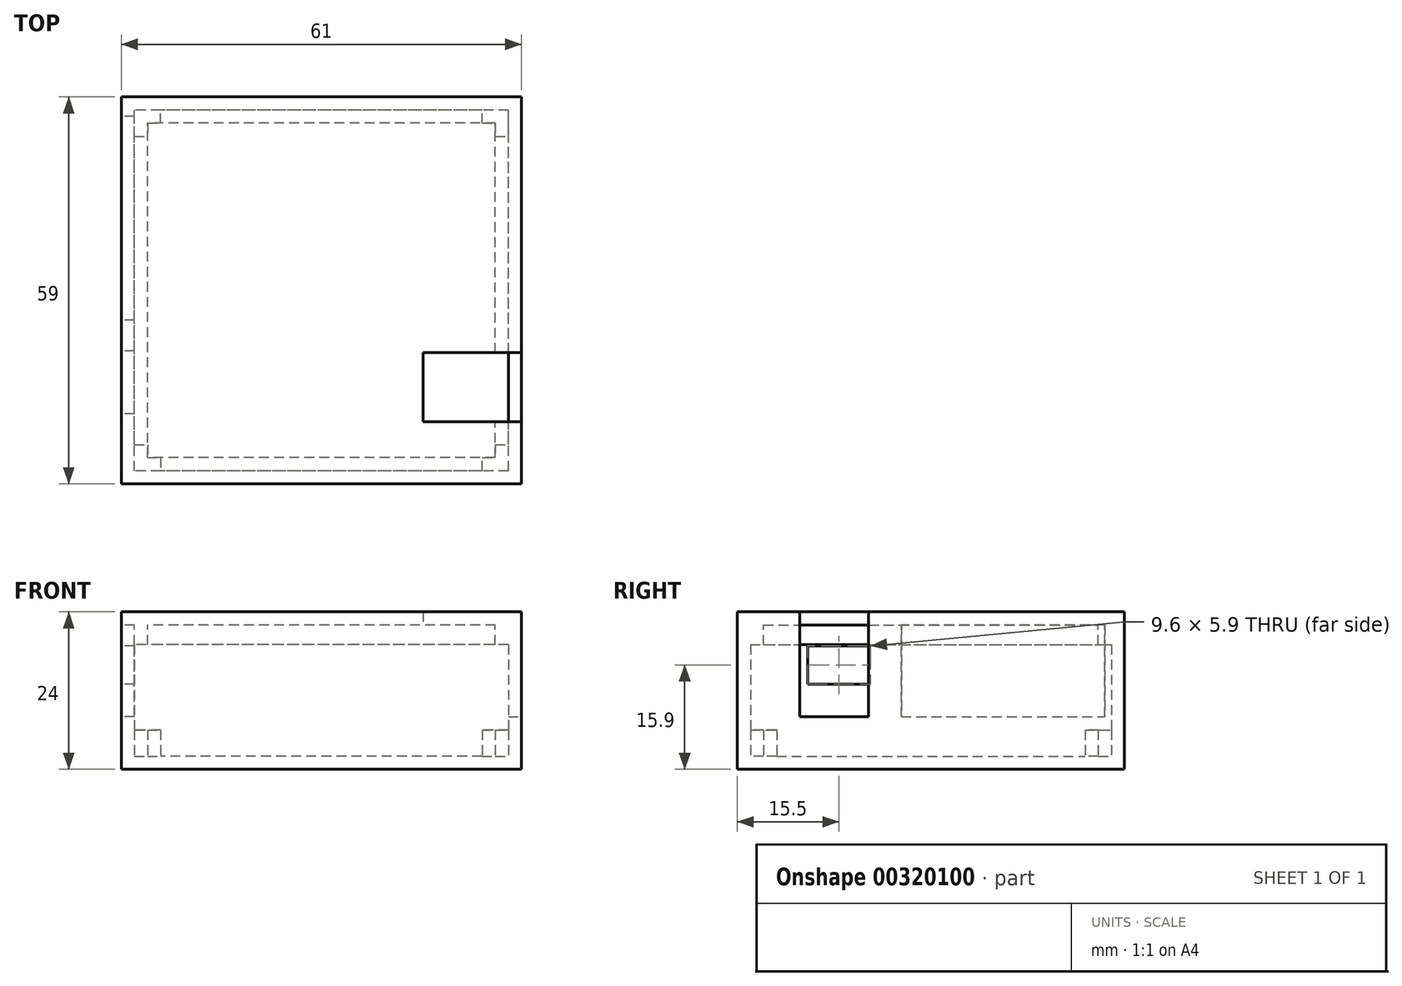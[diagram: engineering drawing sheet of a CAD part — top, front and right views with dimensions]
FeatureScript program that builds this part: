
annotation { "Feature Type Name" : "Feature", "Feature Type Description" : "" }
export const myFeature = defineFeature(function(context is Context, id is Id, definition is map)
    precondition{}
    {
        {
            var Q0;
            Q0=qCreatedBy(makeId("Top.planeOp"),FACE);
            var sketch = newSketch(context, id + "F0", { "sketchPlane" : qUnion([Q0])});
            skLineSegment(sketch, "E0.bottom", {"start": v(28.5, -27.5) * mm, "end": v(-28.5, -27.5) * mm});
            skLineSegment(sketch, "E0.top", {"start": v(28.5, 27.5) * mm, "end": v(-28.5, 27.5) * mm});
            skLineSegment(sketch, "E0.left", {"start": v(28.5, -27.5) * mm, "end": v(28.5, 27.5) * mm});
            skLineSegment(sketch, "E0.right", {"start": v(-28.5, -27.5) * mm, "end": v(-28.5, 27.5) * mm});
            skPoint(sketch, "E0.middle", {"position": v(0, 0) * mm});
            skLineSegment(sketch, "E1.bottom", {"start": v(-30.5, -29.5) * mm, "end": v(30.5, -29.5) * mm});
            skLineSegment(sketch, "E1.top", {"start": v(-30.5, 29.5) * mm, "end": v(30.5, 29.5) * mm});
            skLineSegment(sketch, "E1.left", {"start": v(-30.5, -29.5) * mm, "end": v(-30.5, 29.5) * mm});
            skLineSegment(sketch, "E1.right", {"start": v(30.5, -29.5) * mm, "end": v(30.5, 29.5) * mm});
            skLineSegment(sketch, "E2.bottom", {"start": v(-26.5, 25.5) * mm, "end": v(-24.5, 25.5) * mm});
            skLineSegment(sketch, "E2.top", {"start": v(-26.5, -25.5) * mm, "end": v(-24.5, -25.5) * mm});
            skLineSegment(sketch, "E2.left", {"start": v(-26.5, 25.5) * mm, "end": v(-26.5, 23.5) * mm});
            skLineSegment(sketch, "E2.right", {"start": v(26.5, 25.5) * mm, "end": v(26.5, 23.5) * mm});
            skLineSegment(sketch, "E3", {"start": v(-30.5, -4.5) * mm, "end": v(-26.5, -4.5) * mm});
            skLineSegment(sketch, "E4", {"start": v(-28.5, 23.5) * mm, "end": v(-26.5, 23.5) * mm});
            skLineSegment(sketch, "E5", {"start": v(-24.5, 25.5) * mm, "end": v(-24.5, 27.5) * mm});
            skLineSegment(sketch, "E6", {"start": v(24.5, 25.5) * mm, "end": v(24.5, 27.5) * mm});
            skLineSegment(sketch, "E7", {"start": v(26.5, 23.5) * mm, "end": v(28.5, 23.5) * mm});
            skLineSegment(sketch, "E8", {"start": v(-28.5, -23.5) * mm, "end": v(-26.5, -23.5) * mm});
            skLineSegment(sketch, "E9", {"start": v(-24.5, -25.5) * mm, "end": v(-24.5, -27.5) * mm});
            skLineSegment(sketch, "E10", {"start": v(26.5, -23.5) * mm, "end": v(28.5, -23.5) * mm});
            skLineSegment(sketch, "E11", {"start": v(24.5, -27.5) * mm, "end": v(24.5, -25.5) * mm});
            skLineSegment(sketch, "E12.trimOffspring", {"start": v(26.5, -23.5) * mm, "end": v(26.5, -25.5) * mm});
            skLineSegment(sketch, "E13.trimOffspring", {"start": v(24.5, 25.5) * mm, "end": v(26.5, 25.5) * mm});
            skLineSegment(sketch, "E14.trimOffspring", {"start": v(-26.5, -23.5) * mm, "end": v(-26.5, -25.5) * mm});
            skLineSegment(sketch, "E15.trimOffspring", {"start": v(24.5, -25.5) * mm, "end": v(26.5, -25.5) * mm});
            skSolve(sketch);
        }
        {
            var Q0;
            Q0=makeQuery(id+"F0.imprint","IMPRINT",FACE,{"disambiguationData":[TD([[makeQuery(id+"F0.imprint","IMPRINT",EDGE,{"derivedFrom":sQuery(id+"F0.wireOp",EDGE,"E0.bottom")}),1.0]])]});
            var Q1;
            Q1=makeQuery(id+"F0.imprint","IMPRINT",FACE,{"disambiguationData":[TD([[makeQuery(id+"F0.imprint","IMPRINT",EDGE,{"derivedFrom":sQuery(id+"F0.wireOp",EDGE,"E0.bottom")}),-1.0]])]});
            var Q2;
            Q2=makeQuery(id+"F0.imprint","IMPRINT",FACE,{"disambiguationData":[TD([[makeQuery(id+"F0.imprint","IMPRINT",EDGE,{"derivedFrom":sQuery(id+"F0.wireOp",EDGE,"E2.bottom")}),-1.0]])]});
            var Q3;
            Q3=makeQuery(id+"F0.imprint","IMPRINT",FACE,{"disambiguationData":[TD([[makeQuery(id+"F0.imprint","IMPRINT",EDGE,{"derivedFrom":sQuery(id+"F0.wireOp",EDGE,"E2.right")}),1.0]])]});
            var Q4;
            Q4=makeQuery(id+"F0.imprint","IMPRINT",FACE,{"disambiguationData":[TD([[makeQuery(id+"F0.imprint","IMPRINT",EDGE,{"derivedFrom":sQuery(id+"F0.wireOp",EDGE,"E2.bottom")}),1.0]])]});
            var Q5;
            Q5=sQuery(id+"F0.wireOp",EDGE,"E1.right");
            var Q6;
            Q6=sQuery(id+"F0.wireOp",EDGE,"E1.top");
            var Q7;
            Q7=sQuery(id+"F0.wireOp",EDGE,"E1.left");
            var Q8;
            Q8=sQuery(id+"F0.wireOp",EDGE,"E1.bottom");
            extrude(context, id + "F1", {"entities" : qUnion([Q0, Q1, Q2, Q3, Q4]), "surfaceEntities" : qUnion([Q5, Q6, Q7, Q8]), "depth" : -2 * mm});
        }
        {
            var Q0;
            Q0 = qSketchRegion(id + "F0", true);
            extrude(context, id + "F2", {"entities" : qUnion([Q0]), "operationType" : NewBodyOperationType.ADD, "depth" : 20 * mm});
        }
        {
            var Q0;
            Q0=qCreatedBy(makeId("Right.planeOp"),FACE);
            cPlane(context, id + "F3", {"entities" : qUnion([Q0]), "cplaneType" : CPlaneType.OFFSET, "offset" : 61 / 2 * mm, "oppositeDirection" : true, "width" : 150 * mm, "height" : 150 * mm});
        }
        {
            var Q0;
            Q0=qCreatedBy(id+"F3.planeOp",FACE);
            var sketch = newSketch(context, id + "F4", { "sketchPlane" : qUnion([Q0])});
            skLineSegment(sketch, "E16.bottom", {"start": v(26.5, 20) * mm, "end": v(-4.5, 20) * mm});
            skLineSegment(sketch, "E16.top", {"start": v(26.5, 6) * mm, "end": v(-4.5, 6) * mm});
            skLineSegment(sketch, "E16.left", {"start": v(26.5, 20) * mm, "end": v(26.5, 6) * mm});
            skLineSegment(sketch, "E16.right", {"start": v(-4.5, 20) * mm, "end": v(-4.5, 6) * mm});
            skLineSegment(sketch, "E17.bottom", {"start": v(-18.8, 10.95) * mm, "end": v(-9.2, 10.95) * mm});
            skLineSegment(sketch, "E17.top", {"start": v(-18.8, 16.85) * mm, "end": v(-9.2, 16.85) * mm});
            skLineSegment(sketch, "E17.left", {"start": v(-18.8, 10.95) * mm, "end": v(-18.8, 16.85) * mm});
            skLineSegment(sketch, "E17.right", {"start": v(-9.2, 10.95) * mm, "end": v(-9.2, 16.85) * mm});
            skPoint(sketch, "E17.middle", {"position": v(-14, 13.9) * mm});
            skSolve(sketch);
        }
        {
            var Q0;
            Q0=makeQuery(id+"F4.imprint","IMPRINT",FACE,{"disambiguationData":[TD([[makeQuery(id+"F4.imprint","IMPRINT",EDGE,{"derivedFrom":sQuery(id+"F4.wireOp",EDGE,"E16.bottom")}),1.0]])]});
            extrude(context, id + "F5", {"entities" : qUnion([Q0]), "operationType" : NewBodyOperationType.REMOVE, "endBound" : BoundingType.UP_TO_NEXT, "depth" : 19 * mm});
        }
        {
            var Q0;
            Q0=qCreatedBy(makeId("Right.planeOp"),FACE);
            cPlane(context, id + "F6", {"entities" : qUnion([Q0]), "cplaneType" : CPlaneType.OFFSET, "offset" : 30.5 * mm, "width" : 150 * mm, "height" : 150 * mm});
        }
        {
            var Q0;
            Q0=qCreatedBy(id+"F6.planeOp",FACE);
            var sketch = newSketch(context, id + "F7", { "sketchPlane" : qUnion([Q0])});
            skLineSegment(sketch, "E18.bottom", {"start": v(-20, 20) * mm, "end": v(-9.5, 20) * mm});
            skLineSegment(sketch, "E18.top", {"start": v(-20, 6) * mm, "end": v(-9.5, 6) * mm});
            skLineSegment(sketch, "E18.left", {"start": v(-20, 20) * mm, "end": v(-20, 6) * mm});
            skLineSegment(sketch, "E18.right", {"start": v(-9.5, 20) * mm, "end": v(-9.5, 6) * mm});
            skSolve(sketch);
        }
        {
            var Q0;
            Q0=makeQuery(id+"F7.imprint","IMPRINT",FACE,{"disambiguationData":[TD([[makeQuery(id+"F7.imprint","IMPRINT",EDGE,{"derivedFrom":sQuery(id+"F7.wireOp",EDGE,"E18.bottom")}),-1.0]])]});
            extrude(context, id + "F8", {"entities" : qUnion([Q0]), "operationType" : NewBodyOperationType.REMOVE, "endBound" : BoundingType.UP_TO_NEXT, "oppositeDirection" : true, "depth" : 7 * mm});
        }
        {
            var Q0;
            Q0=makeQuery(id+"F4.imprint","IMPRINT",FACE,{"disambiguationData":[TD([[makeQuery(id+"F4.imprint","IMPRINT",EDGE,{"derivedFrom":sQuery(id+"F4.wireOp",EDGE,"E17.bottom")}),1.0]])]});
            extrude(context, id + "F9", {"entities" : qUnion([Q0]), "operationType" : NewBodyOperationType.REMOVE, "depth" : 25 * mm});
        }
        {
            var Q0;
            Q0=qCreatedBy(makeId("Top.planeOp"),FACE);
            cPlane(context, id + "F10", {"entities" : qUnion([Q0]), "cplaneType" : CPlaneType.OFFSET, "offset" : 20 * mm, "width" : 150 * mm, "height" : 150 * mm});
        }
        {
            var Q0;
            Q0=qCreatedBy(id+"F10.planeOp",FACE);
            var sketch = newSketch(context, id + "F11", { "sketchPlane" : qUnion([Q0])});
            skLineSegment(sketch, "E19.bottom", {"start": v(28.5, -27.5) * mm, "end": v(-28.5, -27.5) * mm});
            skLineSegment(sketch, "E19.top", {"start": v(28.5, 27.5) * mm, "end": v(-28.5, 27.5) * mm});
            skLineSegment(sketch, "E19.left", {"start": v(28.5, -27.5) * mm, "end": v(28.5, 27.5) * mm});
            skLineSegment(sketch, "E19.right", {"start": v(-28.5, -27.5) * mm, "end": v(-28.5, 27.5) * mm});
            skPoint(sketch, "E19.middle", {"position": v(0, 0) * mm});
            skLineSegment(sketch, "E20.bottom", {"start": v(30.5, 29.5) * mm, "end": v(-30.5, 29.5) * mm});
            skLineSegment(sketch, "E20.top", {"start": v(30.5, -29.5) * mm, "end": v(-30.5, -29.5) * mm});
            skLineSegment(sketch, "E20.left", {"start": v(30.5, 29.5) * mm, "end": v(30.5, -29.5) * mm});
            skLineSegment(sketch, "E20.right", {"start": v(-30.5, 29.5) * mm, "end": v(-30.5, -29.5) * mm});
            skLineSegment(sketch, "E21.bottom", {"start": v(26.5, -25.5) * mm, "end": v(-26.5, -25.5) * mm});
            skLineSegment(sketch, "E21.top", {"start": v(26.5, 25.5) * mm, "end": v(-26.5, 25.5) * mm});
            skLineSegment(sketch, "E21.left", {"start": v(26.5, -25.5) * mm, "end": v(26.5, 25.5) * mm});
            skLineSegment(sketch, "E21.right", {"start": v(-26.5, -25.5) * mm, "end": v(-26.5, 25.5) * mm});
            skLineSegment(sketch, "E22.bottom", {"start": v(30.5, -9.5) * mm, "end": v(15.5, -9.5) * mm});
            skLineSegment(sketch, "E22.top", {"start": v(30.5, -20) * mm, "end": v(15.5, -20) * mm});
            skLineSegment(sketch, "E22.left", {"start": v(30.5, -9.5) * mm, "end": v(30.5, -20) * mm});
            skLineSegment(sketch, "E22.right", {"start": v(15.5, -9.5) * mm, "end": v(15.5, -20) * mm});
            skLineSegment(sketch, "E23.bottom", {"start": v(-28.5, 27.5) * mm, "end": v(-18.5, 27.5) * mm});
            skLineSegment(sketch, "E23.top", {"start": v(-28.5, -4.5) * mm, "end": v(-18.5, -4.5) * mm});
            skLineSegment(sketch, "E23.left", {"start": v(-28.5, 27.5) * mm, "end": v(-28.5, -4.5) * mm});
            skLineSegment(sketch, "E23.right", {"start": v(-18.5, 27.5) * mm, "end": v(-18.5, -4.5) * mm});
            skSolve(sketch);
        }
        {
            var Q0;
            Q0=makeQuery(id+"F11.imprint","IMPRINT",FACE,{"disambiguationData":[TD([[makeQuery(id+"F11.imprint","IMPRINT",EDGE,{"derivedFrom":sQuery(id+"F11.wireOp",EDGE,"E19.bottom")}),1.0]])]});
            var Q1;
            Q1=makeQuery(id+"F11.imprint","IMPRINT",FACE,{"disambiguationData":[TD([[makeQuery(id+"F11.imprint","IMPRINT",EDGE,{"derivedFrom":sQuery(id+"F11.wireOp",EDGE,"E21.bottom")}),-1.0]])]});
            var Q2;
            Q2=makeQuery(id+"F11.imprint","IMPRINT",FACE,{"disambiguationData":[TD([[makeQuery(id+"F11.imprint","IMPRINT",EDGE,{"derivedFrom":sQuery(id+"F11.wireOp",EDGE,"E19.bottom")}),-1.0]])]});
            var Q3;
            {var subQ0=sQuery(id+"F11.wireOp",EDGE,"E21.right");var subQ1=sQuery(id+"F11.wireOp",EDGE,"E21.top");var subQ2=makeQuery(id+"F11.imprint","INTERSECT",VERTEX,{"derivedFrom":[subQ1,subQ0]});Q3=makeQuery(id+"F11.imprint","IMPRINT",FACE,{"disambiguationData":[TD([[makeQuery(id+"F11.imprint","IMPRINT",EDGE,{"disambiguationData":[TD([[subQ2,1.0]])],"derivedFrom":subQ1}),1.0]])]});}
            var Q4;
            {var subQ0=sQuery(id+"F11.wireOp",EDGE,"E23.bottom");Q4=makeQuery(id+"F11.imprint","IMPRINT",FACE,{"disambiguationData":[TD([[makeQuery(id+"F11.imprint","IMPRINT",EDGE,{"derivedFrom":subQ0}),-1.0]])]});}
            var Q5;
            {var subQ5=sQuery(id+"F11.wireOp",EDGE,"E19.top");Q5=makeQuery(id+"F11.imprint","IMPRINT",FACE,{"disambiguationData":[TD([[makeQuery(id+"F11.imprint","IMPRINT",EDGE,{"derivedFrom":subQ5}),1.0]])]});}
            extrude(context, id + "F12", {"entities" : qUnion([Q0, Q1, Q2, Q3, Q4, Q5]), "depth" : 2 * mm});
        }
        {
            var Q0;
            Q0=makeQuery(id+"F11.imprint","IMPRINT",FACE,{"disambiguationData":[TD([[makeQuery(id+"F11.imprint","IMPRINT",EDGE,{"derivedFrom":sQuery(id+"F11.wireOp",EDGE,"E19.bottom")}),-1.0]])]});
            var Q1;
            {var subQ0=sQuery(id+"F11.wireOp",EDGE,"E23.bottom");Q1=makeQuery(id+"F11.imprint","IMPRINT",FACE,{"disambiguationData":[TD([[makeQuery(id+"F11.imprint","IMPRINT",EDGE,{"derivedFrom":subQ0}),-1.0]])]});}
            var Q2;
            {var subQ5=sQuery(id+"F11.wireOp",EDGE,"E19.top");Q2=makeQuery(id+"F11.imprint","IMPRINT",FACE,{"disambiguationData":[TD([[makeQuery(id+"F11.imprint","IMPRINT",EDGE,{"derivedFrom":subQ5}),1.0]])]});}
            extrude(context, id + "F13", {"entities" : qUnion([Q0, Q1, Q2]), "operationType" : NewBodyOperationType.ADD, "oppositeDirection" : true, "depth" : 3 * mm});
        }
        {
            var Q0;
            {var subQ0=sQuery(id+"F11.wireOp",EDGE,"E21.right");var subQ1=sQuery(id+"F11.wireOp",EDGE,"E21.top");var subQ2=makeQuery(id+"F11.imprint","INTERSECT",VERTEX,{"derivedFrom":[subQ1,subQ0]});Q0=makeQuery(id+"F11.imprint","IMPRINT",FACE,{"disambiguationData":[TD([[makeQuery(id+"F11.imprint","IMPRINT",EDGE,{"disambiguationData":[TD([[subQ2,1.0]])],"derivedFrom":subQ1}),1.0]])]});}
            var Q1;
            {var subQ0=sQuery(id+"F11.wireOp",EDGE,"E23.bottom");Q1=makeQuery(id+"F11.imprint","IMPRINT",FACE,{"disambiguationData":[TD([[makeQuery(id+"F11.imprint","IMPRINT",EDGE,{"derivedFrom":subQ0}),-1.0]])]});}
            extrude(context, id + "F14", {"entities" : qUnion([Q0, Q1]), "operationType" : NewBodyOperationType.REMOVE, "oppositeDirection" : true, "depth" : 3 * mm});
        }
        {
            var Q0;
            Q0=makeQuery(id+"F0.imprint","IMPRINT",FACE,{"disambiguationData":[TD([[makeQuery(id+"F0.imprint","IMPRINT",EDGE,{"derivedFrom":sQuery(id+"F0.wireOp",EDGE,"E2.right")}),1.0]])]});
            var Q1;
            Q1=makeQuery(id+"F0.imprint","IMPRINT",FACE,{"disambiguationData":[TD([[makeQuery(id+"F0.imprint","IMPRINT",EDGE,{"derivedFrom":sQuery(id+"F0.wireOp",EDGE,"E2.bottom")}),1.0]])]});
            var Q2;
            Q2=makeQuery(id+"F0.imprint","IMPRINT",FACE,{"disambiguationData":[TD([[makeQuery(id+"F0.imprint","IMPRINT",EDGE,{"derivedFrom":sQuery(id+"F0.wireOp",EDGE,"E2.top")}),-1.0]])]});
            var Q3;
            {var subQ1=sQuery(id+"F0.wireOp",EDGE,"E10");Q3=makeQuery(id+"F0.imprint","IMPRINT",FACE,{"disambiguationData":[TD([[makeQuery(id+"F0.imprint","IMPRINT",EDGE,{"derivedFrom":subQ1}),-1.0]])]});}
            extrude(context, id + "F15", {"entities" : qUnion([Q0, Q1, Q2, Q3]), "operationType" : NewBodyOperationType.ADD, "depth" : 4 * mm});
        }
    });
